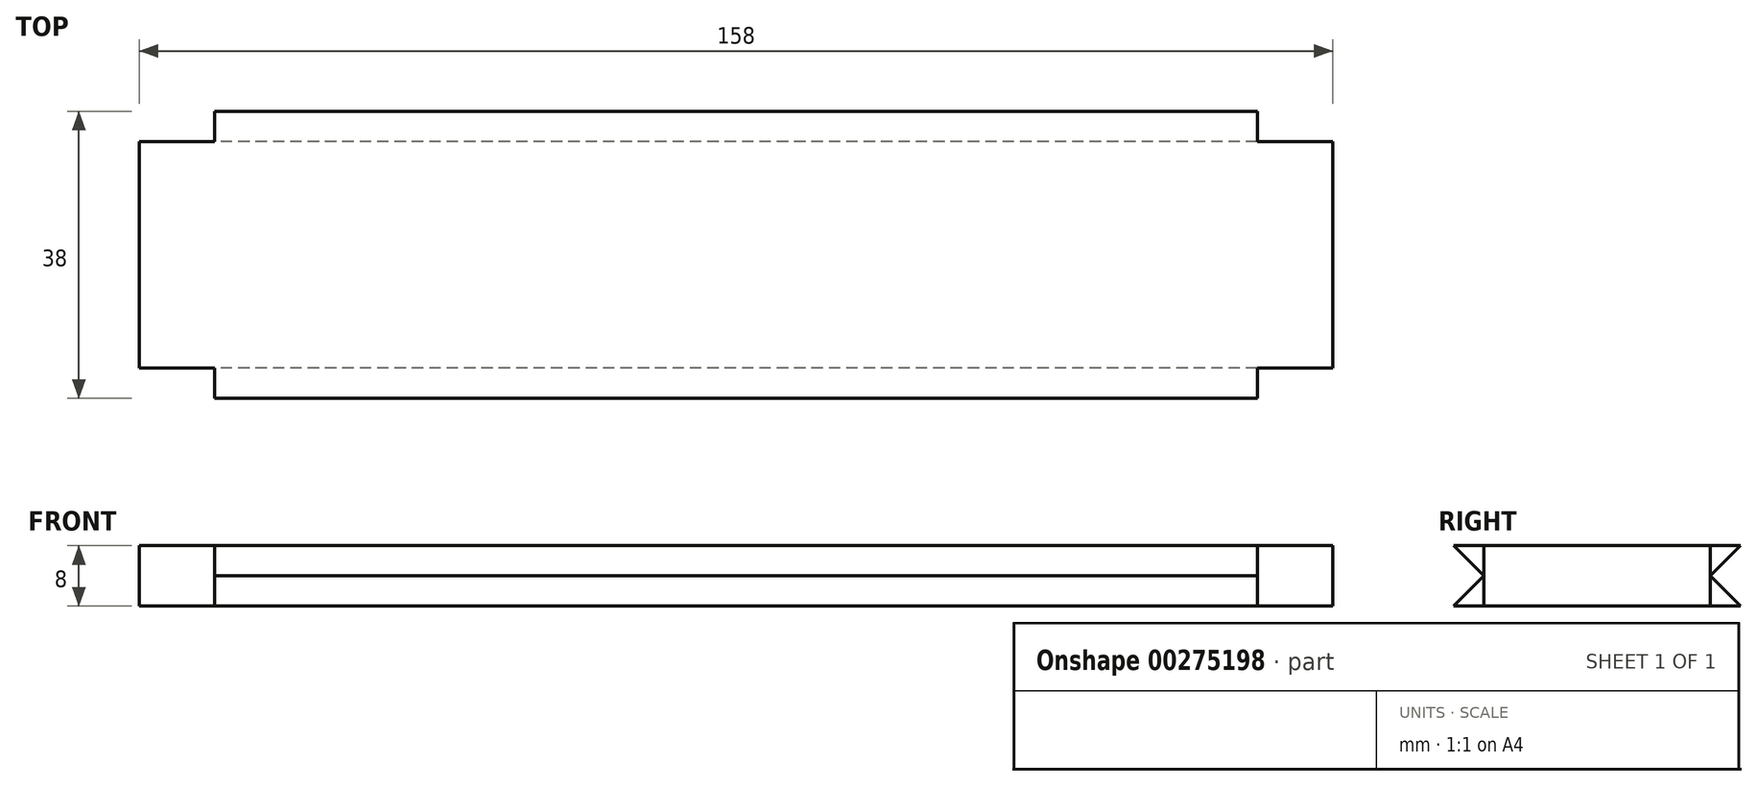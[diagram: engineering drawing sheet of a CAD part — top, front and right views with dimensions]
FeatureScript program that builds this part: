
annotation { "Feature Type Name" : "Feature", "Feature Type Description" : "" }
export const myFeature = defineFeature(function(context is Context, id is Id, definition is map)
    precondition{}
    {
        {
            var Q0;
            Q0=qCreatedBy(makeId("Top.planeOp"),FACE);
            var sketch = newSketch(context, id + "F0", { "sketchPlane" : qUnion([Q0])});
            skLineSegment(sketch, "E0", {"start": v(-85.7, 7.32) * mm, "end": v(-75.7, 7.32) * mm});
            skLineSegment(sketch, "E1", {"start": v(-75.7, 7.32) * mm, "end": v(-75.7, 11.32) * mm});
            skLineSegment(sketch, "E2", {"start": v(-75.7, 11.32) * mm, "end": v(62.3, 11.32) * mm});
            skLineSegment(sketch, "E3", {"start": v(62.3, 11.32) * mm, "end": v(62.3, 7.32) * mm});
            skLineSegment(sketch, "E4", {"start": v(62.3, 7.32) * mm, "end": v(72.3, 7.32) * mm});
            skLineSegment(sketch, "E5", {"start": v(72.3, 7.32) * mm, "end": v(72.3, -22.68) * mm});
            skLineSegment(sketch, "E6", {"start": v(72.3, -22.68) * mm, "end": v(62.3, -22.68) * mm});
            skLineSegment(sketch, "E7", {"start": v(62.3, -22.68) * mm, "end": v(62.3, -26.68) * mm});
            skLineSegment(sketch, "E8", {"start": v(62.3, -26.68) * mm, "end": v(-75.7, -26.68) * mm});
            skLineSegment(sketch, "E9", {"start": v(-75.7, -26.68) * mm, "end": v(-75.7, -22.68) * mm});
            skLineSegment(sketch, "E10", {"start": v(-75.7, -22.68) * mm, "end": v(-85.7, -22.68) * mm});
            skLineSegment(sketch, "E11", {"start": v(-85.7, -22.68) * mm, "end": v(-85.7, 7.32) * mm});
            skSolve(sketch);
        }
        {
            var Q0;
            Q0=makeQuery(id+"F0.imprint","IMPRINT",FACE,{"disambiguationData":[TD([[makeQuery(id+"F0.imprint","IMPRINT",EDGE,{"derivedFrom":sQuery(id+"F0.wireOp",EDGE,"E0")}),-1.0]])]});
            extrude(context, id + "F1", {"entities" : qUnion([Q0]), "depth" : 8 * mm});
        }
        {
            var Q0;
            Q0=makeQuery(id+"F1.opExtrude","SWEPT_FACE",FACE,{"disambiguationData":[OSD([sQuery(id+"F0.wireOp",EDGE,"E9")])]});
            var sketch = newSketch(context, id + "F2", { "sketchPlane" : qUnion([Q0])});
            skLineSegment(sketch, "E12", {"start": v(26.68, 0) * mm, "end": v(22.68, 4) * mm});
            skPoint(sketch, "E12.endSnap0", {"position": v(26.68, 4) * mm});
            skLineSegment(sketch, "E13", {"start": v(22.68, 4) * mm, "end": v(26.68, 8) * mm});
            skSolve(sketch);
        }
        {
            var Q0;
            Q0=makeQuery(id+"F1.opExtrude","SWEPT_FACE",FACE,{"disambiguationData":[OSD([sQuery(id+"F0.wireOp",EDGE,"E1")])]});
            var sketch = newSketch(context, id + "F3", { "sketchPlane" : qUnion([Q0])});
            skLineSegment(sketch, "E14", {"start": v(-11.32, 8) * mm, "end": v(-7.32, 4) * mm});
            skPoint(sketch, "E14.endSnap0", {"position": v(-11.32, 4) * mm});
            skLineSegment(sketch, "E15", {"start": v(-7.32, 4) * mm, "end": v(-11.32, 0) * mm});
            skSolve(sketch);
        }
        {
            var Q0;
            Q0=makeQuery(id+"F2.imprint","IMPRINT",FACE,{"disambiguationData":[TD([[makeQuery(id+"F2.imprint","IMPRINT",EDGE,{"derivedFrom":sQuery(id+"F2.wireOp",EDGE,"E12")}),-1.0]])]});
            var Q1;
            Q1=makeQuery(id+"F3.imprint","IMPRINT",FACE,{"disambiguationData":[TD([[makeQuery(id+"F3.imprint","IMPRINT",EDGE,{"derivedFrom":sQuery(id+"F3.wireOp",EDGE,"E14")}),-1.0]])]});
            extrude(context, id + "F4", {"entities" : qUnion([Q0, Q1]), "operationType" : NewBodyOperationType.REMOVE, "endBound" : BoundingType.THROUGH_ALL, "oppositeDirection" : true, "depth" : 25 * mm});
        }
    });
